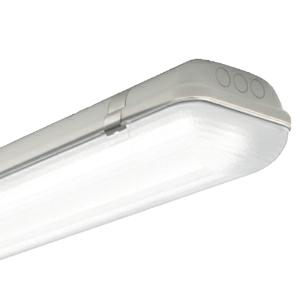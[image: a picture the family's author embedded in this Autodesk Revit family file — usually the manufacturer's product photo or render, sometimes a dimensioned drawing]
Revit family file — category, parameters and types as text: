
# Revit family: 3f_filippi_-_3f_linda_soft_3f_filippi_-_58752_-_3f_linda_led_soft_2x30w_l1570
name_source: partatom
category: Lighting Fixtures
units: mm (PartAtom-declared; Revit-internal decimal feet)

## family parameters
Cut with Voids When Loaded = No
Host = Face
Light Source = No
Part Type = Normal
Room Calculation Point = No
Round Connector Dimension = Use Diameter
Shared = No

## types (1)
- 3F Filippi - 3F Linda Soft (1 x LED, 8788 lm, 66 W, 4000 K)
    Apparent Load = 66 VA
    Approval mark = CE
    CIE Flux Codes = 42 72 91 93 100
    Color Rendering = 80
    Color Temperature = 4000 K
    Control Gear = Electronic ballast
    Default Elevation = 1800 mm
    Description = ILLUMINOTECHNICAL
Luminous efficiency 100% (DLOR 93%, ULOR 7%).
Initial luminous flux of the luminaire 8788 lm.
Direct symmetric distribution.
Installation Interdistance Transv.D = 1.35 x hu - Long.D = 1.24 x hu.
Tabular UGR (CIE 117 - 4H-8H; S=0.25H; 70/50/20): RUG 24.5 - 22.7.
Beam angle: 131° - 111°.
Luminous efficacy 133 lm/W.
Lifetime (L93/B10): 30000 h. (tq+25°C)
Lifetime (L90/B10): 50000 h. (tq+25°C)
Lifetime (L85/B10): 80000 h. (tq+25°C)
Lifetime (L80/B10): 100000 h. (tq+25°C)
Lifetime (L85/B10): 50000 h. (tq+35°C)
Sudden decreased luminous flux after 50000 hours: 0% (C0).
Photobiological safety in compliance with IEC/TR 62778: RG0 risk exempt, (IEC 62471).
In compliance with IEC/EN 62722-2-1 - IEC/EN 62717 standards.

SOURCE
2 linear LED modules 30W/840.
Energy efficiency class (UE 2019/2020 - UE 2019/2015): D.
CIE 13.3 Colour rendering index: CRI >80 (R9 <50%).
IES TM-30 Fidelity Index: Rf = 84 Rg = 95.
CCT nominal colour temperature 4000 K.
Colour initial tolerance (MacAdam): SDCM 3.

MECHANICAL
Self-extinguishing V2 polycarbonate housing, injection moulded, RAL 7035 grey.
Ecologic anti-aging injected sealing gasket.
Soft opal diffuser in self-extinguishing V2 polycarbonate, photo-engraved interior, UV stabilised, injection moulded.
Gear-holder reflector in hot-dip galvanised steel, painted with white polyester base.
Snug fit safety snap-lock clips for diffuser mounting in stainless steel, screwdriver opening.
Fixing brackets in stainless steel.
Possibility for technicians to access the interior of the luminaire.
Luminaire with limited surface temperature. - D - (EN 60598-2-24)
Dimensions: 1570x160 mm, height 100 mm. Weight 3.47 kg.
IP66 protection degree.
Mechanical strength to impacts IK10 (20 joule).
Glow-wire test resistance 850°C.

ELECTRICAL
Halogen Free electronic wiring 230V-50/60Hz, power factor 0.97, THD <25%, constant output current, SELV, class I, 1 driver.
Power of the luminaire 66 W.
ENEC - CE.
SAFE FLICKER: PstLM=<1 and SVM=<0.4 (IEC TR 61547-1 and IEC TR 63158), to ensure a more comfortable and safe light.
Luminaire compliant with EN 60598-2-22 for power supply from a centralised emergency system CPSS (Central Power Supply System), not incorporated in the luminaire - high risk areas excluded. The default power and flux are 100% in AC and 100% in DC.
Ambient temperature from -20°C to +35°C.
Temperature class T6 max 85°C.
Relative humidity UR: <85%.

INSTALLATION
Ceiling / Suspended / Wall.
All accessories dedicated to this product are available on the Catalog and on our website www.3F-Filippi.com.

APPLICATIONS
Suitable product for food production plants (HACCP), IFS (Food Version 6), BRC (GSFS Food Version 7).
Dry, dusty indoor environments, subject to occasional water splashes.
Luminaires designed for diffuse direct/indirect lighting suitable to provide optimum visual comfort.
Transit areas, stairwells.
Virtually shatterproof polycarbonate compatibly with the fumes / atmospheres that compromise the elasticity of plastic materials.
Suitable for illumination of public car parks and parking grounds referred to DIN 67528:2018-04.

WARNING
Fixture not suitable for cold stores with an ambient temperature <0°C and/or relative humidity >85%.
Luminaire designed for disposal/recycling at end-of-life.
Replaceable (LED only) light source by a professional. Replaceable control gear by a professional.
    Height = 100 mm  [stored 0.328084 ft]
    Lamp = 1 x LED
    Lamp Light Flux = 8788 lm
    Lamp Power = 66 W
    Lamp count = 1
    Length = 1570 mm
    Lifetime = 50000 h
    Luminous efficacy = 133 lm/W
    Manufacturer = 3F Filippi
    ModVariant = No
    Model = 3F Filippi - 58752 - 3F Linda LED Soft 2x30W L1570
    Mounting Place = Ceiling
    Mounting Type = Pendant
    Number of Poles = 1
    OnlyDefault = Yes
    Power Factor = 1
    Product Name = 3F Filippi - 3F Linda Soft
    Product group = pendant luminaire
    ProductGroupID = 9
    Protection Class = Protection class I
    Protection Degree = IP 66
    RLX_Detail_Level = 1
    RLX_Emergency_Light_Flux = 0 lm
    RLX_Emergency_Type = 0
    RLX_Emergency_Type_DB = No
    RlxData = <blob elided: 69073 chars, md5=87318a63>
    Socket = socket
    Standby Power = 0 W
    System Light Flux = 8788 lm
    System Power = 66 W
    Type Comments = Product without accessories
    Type Image = 3ffilippi_3f_linda_led_soft_2x.jpg
    URL = http://relux.com
    VarID = ---
    Voltage = 0 V
    Weight = 0.00 kg
    Width = 160 mm

note: [stored X ft] marks values corroborated as IEEE doubles in the binary element streams (Revit-internal decimal feet)

## geometry (parser evidence)
native form markers: Blend x4, Sweep x11
no freeform markers — native parametric forms only
